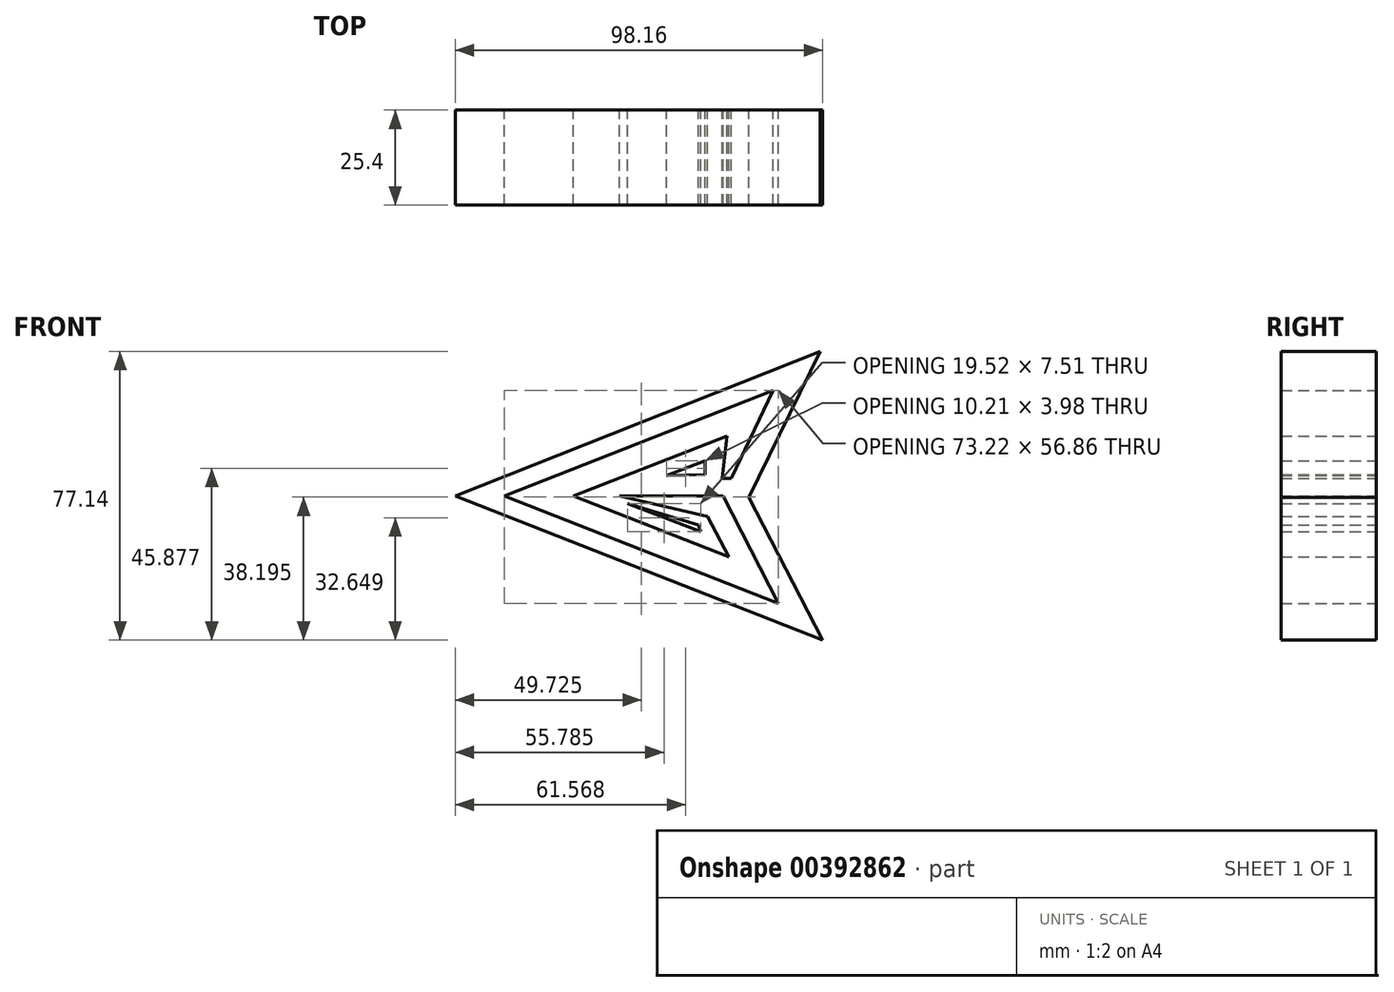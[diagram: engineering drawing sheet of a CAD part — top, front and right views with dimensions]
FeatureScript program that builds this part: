
annotation { "Feature Type Name" : "Feature", "Feature Type Description" : "" }
export const myFeature = defineFeature(function(context is Context, id is Id, definition is map)
    precondition{}
    {
        {
            var Q0;
            Q0=qCreatedBy(makeId("Front.planeOp"),FACE);
            var sketch = newSketch(context, id + "F0", { "sketchPlane" : qUnion([Q0])});
            skLineSegment(sketch, "E0", {"start": v(-59.9, -2.68) * mm, "end": v(37.5, 36.04) * mm});
            skPoint(sketch, "E0.startSnap0", {"position": v(-61.98, -2.68) * mm});
            skLineSegment(sketch, "E1", {"start": v(37.5, 36.04) * mm, "end": v(18.55, -3) * mm});
            skLineSegment(sketch, "E2", {"start": v(18.55, -3) * mm, "end": v(38.26, -41.1) * mm});
            skLineSegment(sketch, "E3", {"start": v(38.26, -41.1) * mm, "end": v(-59.9, -2.68) * mm});
            skLineSegment(sketch, "E4", {"start": v(26.43, -31.34) * mm, "end": v(-46.78, -2.68) * mm});
            skLineSegment(sketch, "E5", {"start": v(-46.78, -2.68) * mm, "end": v(24.93, 25.53) * mm});
            skLineSegment(sketch, "E6", {"start": v(24.93, 25.53) * mm, "end": v(13.86, 2.07) * mm});
            skLineSegment(sketch, "E7", {"start": v(13.86, 2.07) * mm, "end": v(11.42, 2.07) * mm});
            skLineSegment(sketch, "E8", {"start": v(11.42, 2.07) * mm, "end": v(12.73, 13.33) * mm});
            skLineSegment(sketch, "E9", {"start": v(12.73, 13.33) * mm, "end": v(-28.37, -2.68) * mm});
            skLineSegment(sketch, "E10", {"start": v(-28.37, -2.68) * mm, "end": v(13.15, -18.93) * mm});
            skLineSegment(sketch, "E11", {"start": v(13.15, -18.93) * mm, "end": v(7.52, -8.06) * mm});
            skLineSegment(sketch, "E12", {"start": v(7.52, -8.06) * mm, "end": v(-15.98, -2.68) * mm});
            skLineSegment(sketch, "E13", {"start": v(-15.98, -2.68) * mm, "end": v(11.6, -2.68) * mm});
            skLineSegment(sketch, "E14", {"start": v(11.6, -2.68) * mm, "end": v(26.43, -31.34) * mm});
            skLineSegment(sketch, "E15", {"start": v(-3.44, 2.79) * mm, "end": v(6.77, 6.77) * mm});
            skLineSegment(sketch, "E16", {"start": v(6.77, 6.77) * mm, "end": v(6.77, 3.05) * mm});
            skLineSegment(sketch, "E17", {"start": v(6.77, 3.05) * mm, "end": v(-3.44, 2.79) * mm});
            skLineSegment(sketch, "E18", {"start": v(-13.87, -4.7) * mm, "end": v(5.64, -12.2) * mm});
            skLineSegment(sketch, "E19", {"start": v(5.64, -12.2) * mm, "end": v(5.03, -10.42) * mm});
            skLineSegment(sketch, "E20", {"start": v(5.03, -10.42) * mm, "end": v(-13.87, -4.7) * mm});
            skSolve(sketch);
        }
        {
            var Q0;
            Q0=makeQuery(id+"F0.imprint","IMPRINT",FACE,{"disambiguationData":[TD([[makeQuery(id+"F0.imprint","IMPRINT",EDGE,{"derivedFrom":sQuery(id+"F0.wireOp",EDGE,"E0")}),-1.0]])]});
            extrude(context, id + "F1", {"entities" : qUnion([Q0]), "depth" : 25.4 * mm});
        }
    });
